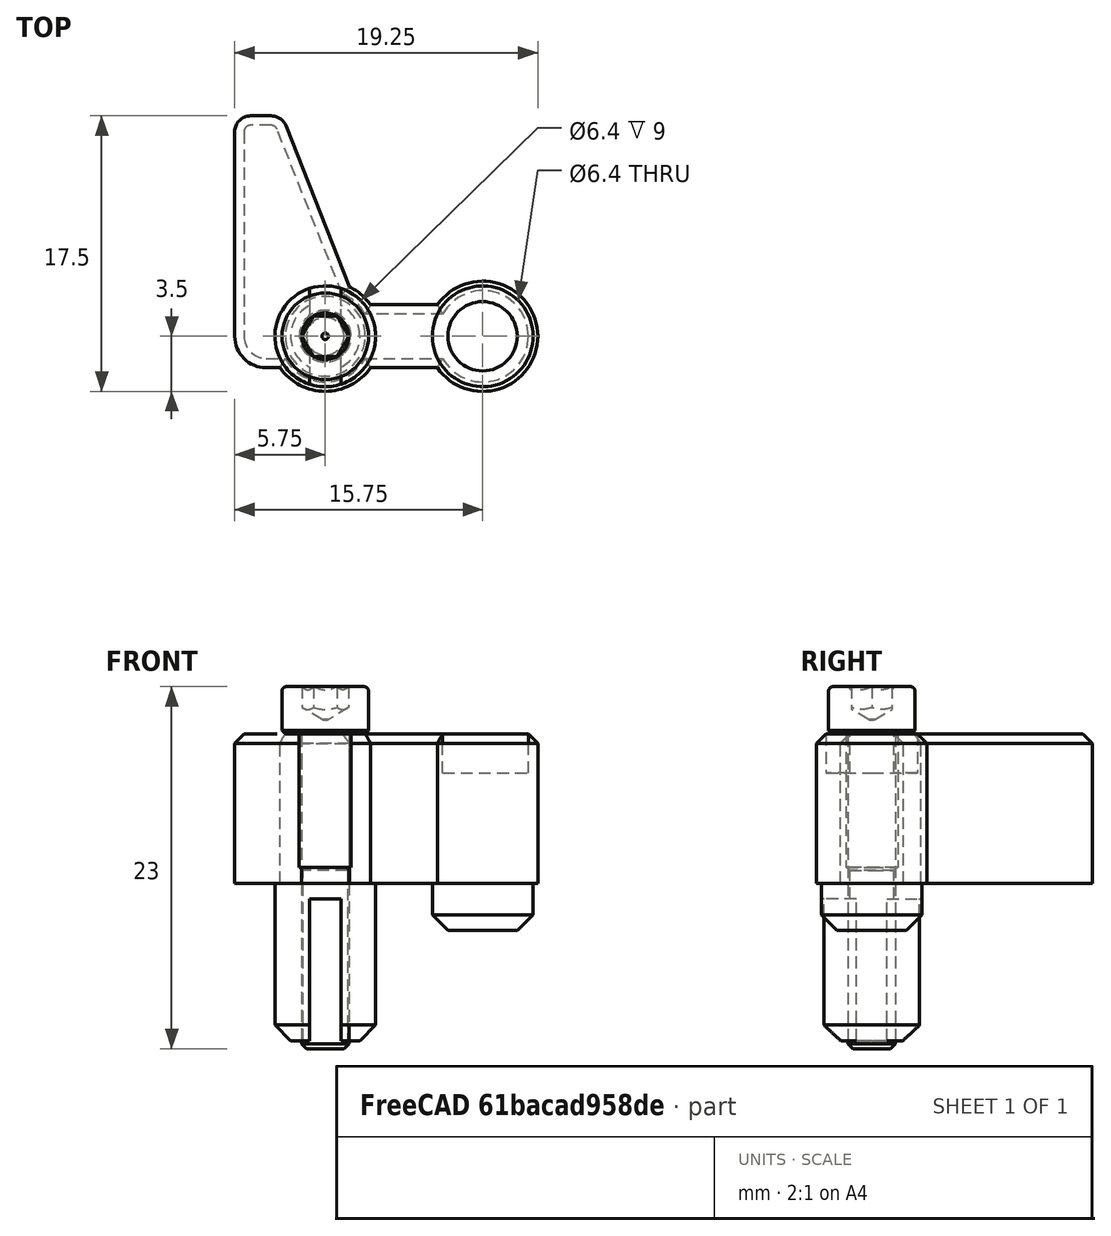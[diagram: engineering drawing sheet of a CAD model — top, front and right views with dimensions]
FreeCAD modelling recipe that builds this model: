
FCSTD DOCUMENT  (FreeCAD 0.19R24291 (Git))
Label: x-endstop-flag-assembly
License: Other
LicenseURL: GPL3
objects: PartDesign::CoordinateSystem×1, Part::Feature×1, Part::FeaturePython×1, App::Part×1
note: 3 computed .brp shape members not serialized (recipe doc carries the construction recipe); baked Part::Feature solids carry a one-line shape summary decoded from their .brp

FEATURE [PartDesign::CoordinateSystem] LCS_x_endstop_flag  label="LCS_x-endstop-flag"
  AttacherType = Attacher::AttachEngine3D
FEATURE [Part::Feature] Pad001  label="1x_x-endstop-flag-1515"
  shape: bbox 19.25 x 17.5 x 19.5 mm, 49 faces (baked)
FEATURE [Part::FeaturePython] Screw  label="M3x20-Screw"  # Fasteners workbench fastener (typed FeaturePython)
  Placement = pos=(0,0,9.5) rot=(0,0,1;0rad)
  baseObject = -> Pad001 [Edge88]
  diameter = 4
  invert = false
  leftHanded = false
  length = 7
  lengthCustom = 20
  matchOuter = false
  offset = 0
  thread = false
  type = 36
FEATURE [App::Part] Part001  label="x-endstop-flag"
  Group = -> [LCS_x_endstop_flag,Pad001,Screw]
  Origin = -> Origin001
